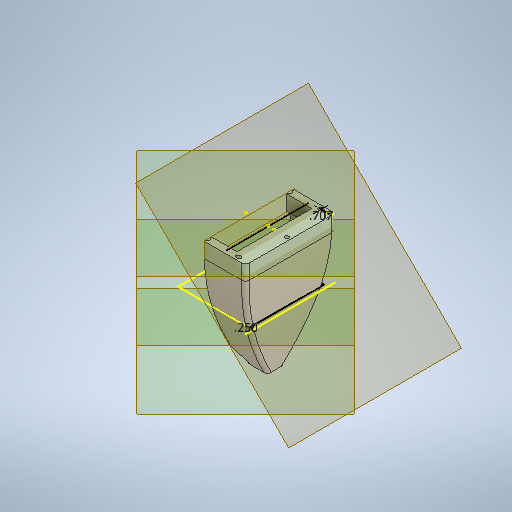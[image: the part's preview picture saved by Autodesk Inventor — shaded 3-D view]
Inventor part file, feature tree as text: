
AUTODESK INVENTOR PART (.ipt)
format: ipt  version: 2025.1 (Build 291241020, 241B)  size: 715,776 bytes
history: native  units: in
note: dims shown in document units (in); Inventor stores cm internally (conversion verified against a paired STEP export)
features: sketch x20, extrude x9, plane x6, fillet x4, loft x1, shell x1, mirror x1, other x1
ambient origin geometry x8: Origin, YZ Plane, XZ Plane, XY Plane, X Axis, Y Axis, Z Axis, Center Point
bodies: Solid1 (feature_tree)
feature tree (43):
  sketch  "Sketch1"  dims[d0=6.0in d1=6.0in]
  plane  "Work Plane1"
  plane  "Work Plane2"
  sketch  "Sketch2"  dims[d2=5.5in d7=8.0in d10=1.0in d11=0.0in d12=4.0in]
  extrude  "Extrusion1"  Depth=6.0in
  sketch  "3D Sketch1"
  plane  "Work Plane3"
  sketch  "Sketch3"  dims[d24=0.6in d25=0.6in]
  loft  "Loft1"
  sketch  "Sketch4"  dims[d26=0.0in d27=90.0deg d28=0.0in d29=90.0deg d30=0.0in d31=90.0deg d32=0.0in d33=90.0deg d38=0.25in d39=0.0in d40=90.0deg]
  fillet  "Fillet1"  Radius=1.0in
  fillet  "Fillet2"  Radius=4.0in
  extrude  "Extrusion3"  Depth=0.6in
  extrude  "Extrusion4"  Depth=0.25in
  shell  "Shell2"  Thickness=0.0in
  extrude  "Extrusion5"  Depth=0.25in
  sketch  "Sketch9"  dims[d64=0.712in d65=0.712in]
  fillet  "Fillet3"  Radius=0.25in
  fillet  "Fillet4"  Radius=0.5in
  extrude  "Extrusion7"  Depth=0.25in
  plane  "Work Plane4"
  sketch  "Sketch10"  dims[d66=0.726in d67=0.1in d68=0.0in]
  sketch  "Sketch11"  dims[d72=0.3in d73=0.25in]
  sketch  "Sketch12"  dims[d76=0.175in]
  extrude  "Extrusion8"  Depth=2.5in
  sketch  "Sketch14"  dims[d78=12.0in d79=0.0in]
  plane  "Work Plane5"
  extrude  "Extrusion9"  Depth=0.712in
  plane  "Work Plane6"
  mirror  "Mirror1"
  extrude  "Extrusion10"  Depth=0.1in TaperAngle=0.0deg
  sketch  "Sketch17"  dims[d83=0.707in]
  sketch  "Sketch18"  dims[d84=45.0deg]
  extrude  "Extrusion11"  Depth=0.3in
  sketch  "3D Sketch7"
  other  "Edges1"
  sketch  "Sketch5"  dims[d41=0.0in d42=90.0deg d44=0.25in d45=0.25in d51=0.5in d52=0.0in]
  sketch  "Sketch7"  dims[d58=0.5in d59=0.0in d60=0.25in]
  sketch  "Sketch8"  dims[d61=2.5in d62=2.5in]
  sketch  "Sketch13"  dims[d77=0.175in]
  sketch  "Sketch15"  dims[d80=1.0in]
  sketch  "Sketch16"  dims[d81=1.0in d82=0.0in]
  sketch  "Sketch19"  dims[d85=0.25in d86=1.0in d87=0.75in d88=0.0in d89=0.0in d90=-2.75in d91=0.175in d92=1.0in d93=1.0in d94=0.205in d95=0.205in d96=0.205in d97=0.205in d98=0.157in d99=0.0in d102=0.7in d103=0.3in d106=0.502in d107=0.502in d108=1.004in d109=0.205in d110=0.205in d111=0.205in d112=0.205in d113=0.157in d114=0.0in d115=2.5in d53=0.5in d54=0.0344in d74=0.0in d75=0.0in]
